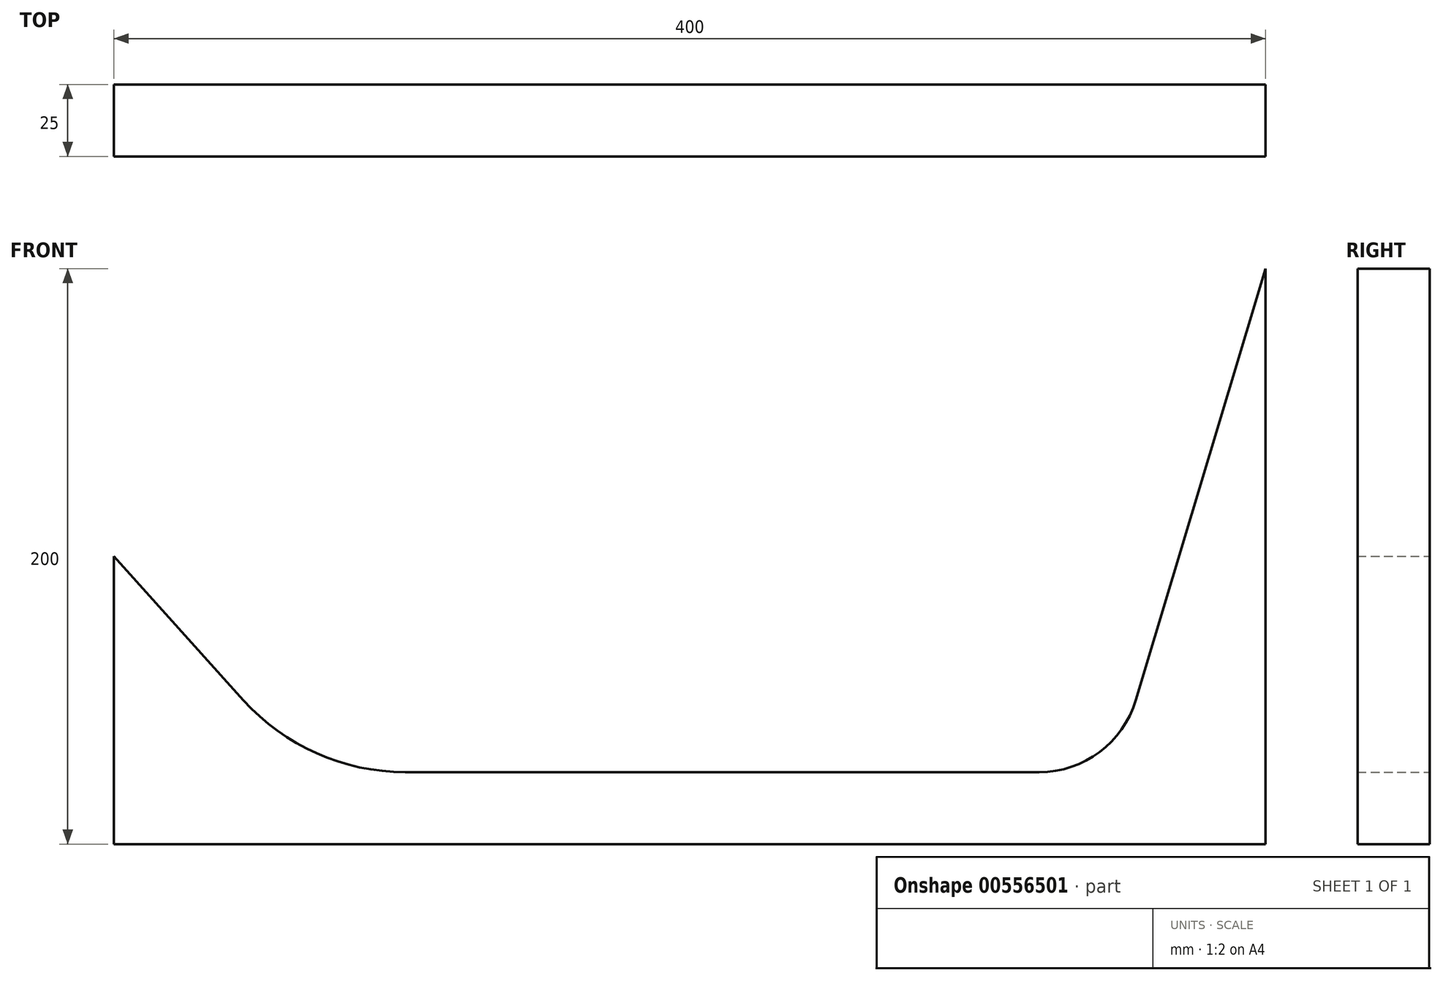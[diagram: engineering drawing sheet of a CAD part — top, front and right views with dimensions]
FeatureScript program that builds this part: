
annotation { "Feature Type Name" : "Feature", "Feature Type Description" : "" }
export const myFeature = defineFeature(function(context is Context, id is Id, definition is map)
    precondition{}
    {
        {
            var Q0;
            Q0=qCreatedBy(makeId("Front.planeOp"),FACE);
            var sketch = newSketch(context, id + "F0", { "sketchPlane" : qUnion([Q0])});
            skLineSegment(sketch, "E0", {"start": v(-200, 0) * mm, "end": v(200, 0) * mm});
            skLineSegment(sketch, "E1", {"start": v(200, 0) * mm, "end": v(200, 200) * mm});
            skLineSegment(sketch, "E2", {"start": v(200, 200) * mm, "end": v(155, 50) * mm});
            skArc(sketch, "E3", {"start": v(155, 50) * mm, "mid": v(142.34, 31.94) * mm, "end": v(121.4, 25) * mm});
            skLineSegment(sketch, "E4", {"start": v(121.4, 25) * mm, "end": v(-98.87, 25) * mm});
            skLineSegment(sketch, "E5", {"start": v(-200, 100) * mm, "end": v(-155, 50) * mm});
            skLineSegment(sketch, "E6", {"start": v(-200, 100) * mm, "end": v(-200, 0) * mm});
            skArc(sketch, "E7", {"start": v(-98.87, 25) * mm, "mid": v(-129.6, 31.53) * mm, "end": v(-155, 50) * mm});
            skLineSegment(sketch, "E8", {"start": v(0, 0) * mm, "end": v(0, 146.81) * mm, "construction": true});
            skLineSegment(sketch, "E9", {"start": v(155, 50) * mm, "end": v(74.55, 50) * mm, "construction": true});
            skSolve(sketch);
        }
        {
            var Q0;
            Q0 = qSketchRegion(id + "F0", true);
            extrude(context, id + "F1", {"entities" : qUnion([Q0]), "depth" : 25 * mm, "offsetDistance" : 25 * mm});
        }
    });
